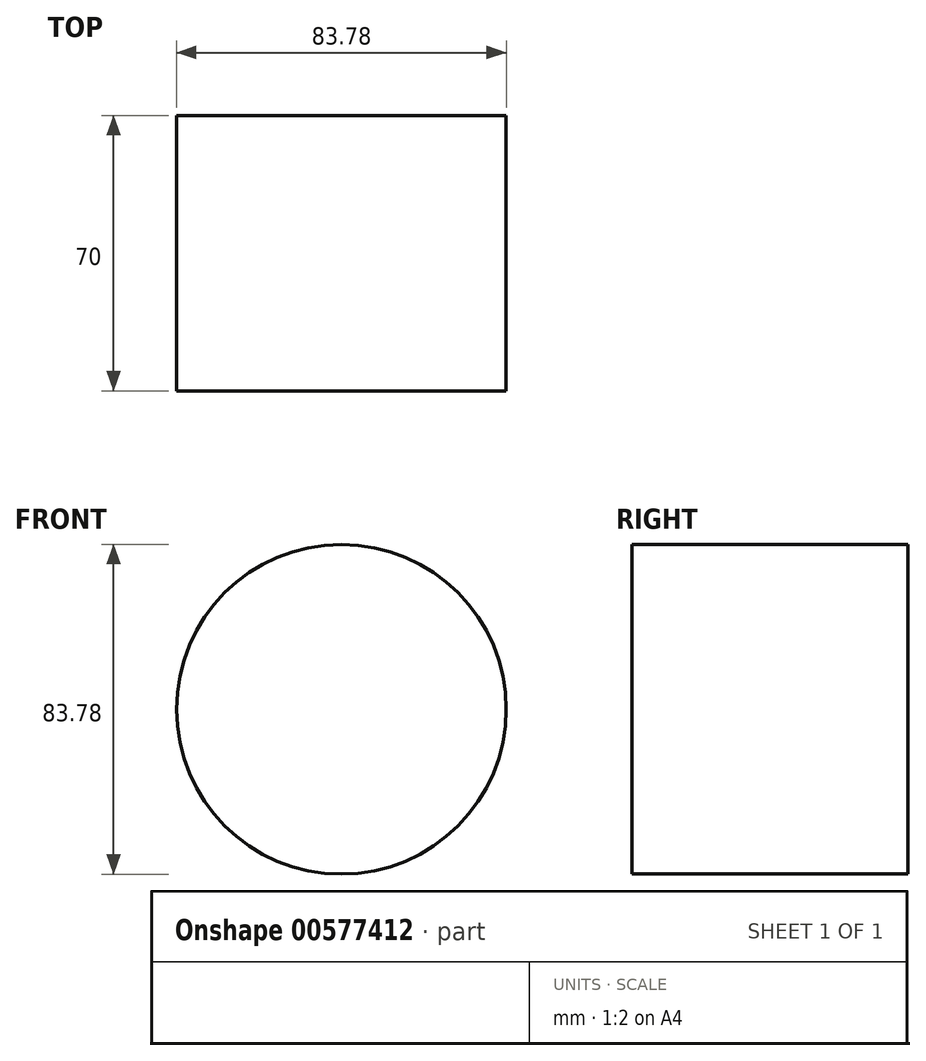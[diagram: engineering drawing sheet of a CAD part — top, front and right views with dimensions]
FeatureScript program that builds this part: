
annotation { "Feature Type Name" : "Feature", "Feature Type Description" : "" }
export const myFeature = defineFeature(function(context is Context, id is Id, definition is map)
    precondition{}
    {
        {
            var Q0;
            Q0=qCreatedBy(makeId("Front.planeOp"),FACE);
            var sketch = newSketch(context, id + "F0", { "sketchPlane" : qUnion([Q0])});
            skCircle(sketch, "E0", {"center": v(0, 0) * mm, "radius": 41.89 * mm});
            skSolve(sketch);
        }
        {
            var Q0;
            Q0=makeQuery(id+"F0.imprint","IMPRINT",FACE,{"disambiguationData":[TD([[makeQuery(id+"F0.imprint","IMPRINT",EDGE,{"derivedFrom":sQuery(id+"F0.wireOp",EDGE,"E0")}),1.0]])]});
            extrude(context, id + "F1", {"entities" : qUnion([Q0]), "depth" : 70 * mm, "offsetDistance" : 25 * mm});
        }
    });
